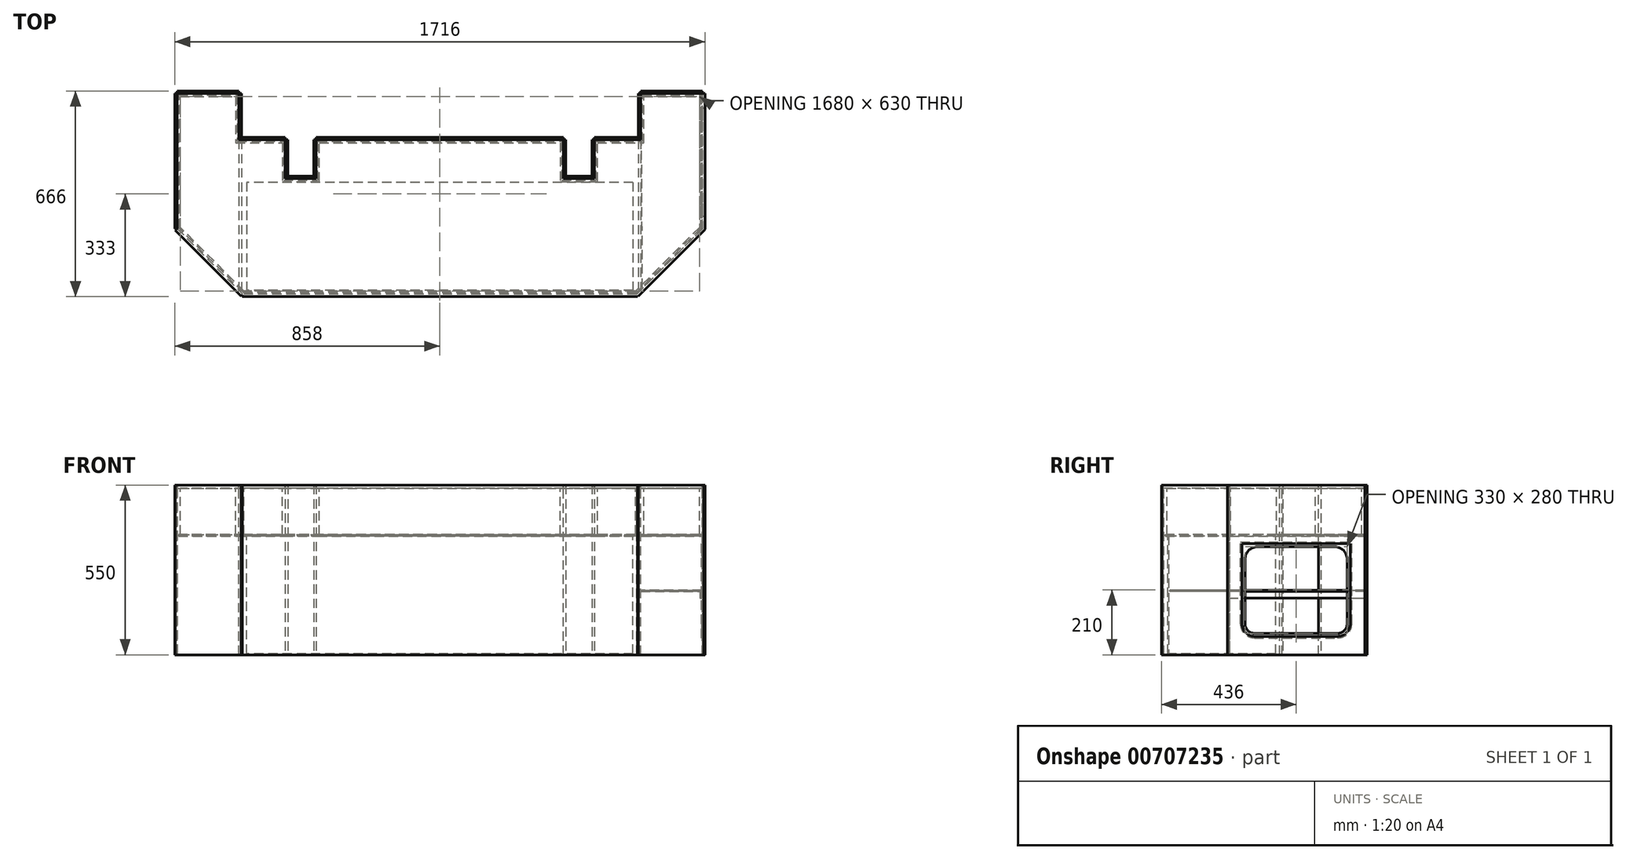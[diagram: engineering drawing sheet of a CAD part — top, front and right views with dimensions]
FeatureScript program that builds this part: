
annotation { "Feature Type Name" : "Feature", "Feature Type Description" : "" }
export const myFeature = defineFeature(function(context is Context, id is Id, definition is map)
    precondition{}
    {
        {
            var Q0;
            Q0=qCreatedBy(makeId("Top.planeOp"),FACE);
            var sketch = newSketch(context, id + "F0", { "sketchPlane" : qUnion([Q0])});
            skLineSegment(sketch, "E0.bottom", {"start": v(650, 250) * mm, "end": v(500, 250) * mm});
            skLineSegment(sketch, "E0.top", {"start": v(637.5, -250) * mm, "end": v(-637.5, -250) * mm});
            skLineSegment(sketch, "E0.left", {"start": v(850, 250) * mm, "end": v(850, -37.5) * mm});
            skLineSegment(sketch, "E0.right", {"start": v(-850, 250) * mm, "end": v(-850, -37.5) * mm});
            skPoint(sketch, "E0.middle", {"position": v(0, 0) * mm});
            skLineSegment(sketch, "E1.top", {"start": v(-850, 400) * mm, "end": v(-650, 400) * mm});
            skLineSegment(sketch, "E1.left", {"start": v(-850, 250) * mm, "end": v(-850, 400) * mm});
            skLineSegment(sketch, "E1.right", {"start": v(-650, 250) * mm, "end": v(-650, 400) * mm});
            skLineSegment(sketch, "E2", {"start": v(0, 547.12) * mm, "end": v(0, -339.99) * mm, "construction": true});
            skLineSegment(sketch, "E3.MirrorCS", {"start": v(850, 250) * mm, "end": v(850, 400) * mm});
            skLineSegment(sketch, "E4.MirrorCS", {"start": v(850, 400) * mm, "end": v(650, 400) * mm});
            skLineSegment(sketch, "E5.MirrorCS", {"start": v(650, 250) * mm, "end": v(650, 400) * mm});
            skLineSegment(sketch, "E6", {"start": v(-400, 250) * mm, "end": v(-400, 125) * mm});
            skLineSegment(sketch, "E7", {"start": v(-400, 125) * mm, "end": v(-500, 125) * mm});
            skLineSegment(sketch, "E8", {"start": v(-500, 125) * mm, "end": v(-500, 250) * mm});
            skLineSegment(sketch, "E9.MirrorCS", {"start": v(400, 250) * mm, "end": v(400, 125) * mm});
            skLineSegment(sketch, "E10.MirrorCS", {"start": v(400, 125) * mm, "end": v(500, 125) * mm});
            skLineSegment(sketch, "E11.MirrorCS", {"start": v(500, 125) * mm, "end": v(500, 250) * mm});
            skLineSegment(sketch, "E12", {"start": v(637.5, -62.5) * mm, "end": v(-637.5, -62.5) * mm, "construction": true});
            skLineSegment(sketch, "E13.top", {"start": v(900, -250) * mm, "end": v(850, -250) * mm, "construction": true});
            skPoint(sketch, "E13.middle", {"position": v(0, -62.5) * mm});
            skLineSegment(sketch, "E14", {"start": v(637.5, 90) * mm, "end": v(637.5, -250) * mm, "construction": true});
            skLineSegment(sketch, "E15", {"start": v(-637.5, 90) * mm, "end": v(-637.5, -250) * mm, "construction": true});
            skLineSegment(sketch, "E16.trimOffspring", {"start": v(400, 250) * mm, "end": v(-400, 250) * mm});
            skLineSegment(sketch, "E17.trimOffspring", {"start": v(-500, 250) * mm, "end": v(-650, 250) * mm});
            skPoint(sketch, "E18.orphan", {"position": v(-850, -250) * mm});
            skLineSegment(sketch, "E19.trimOffspring", {"start": v(637.5, -250) * mm, "end": v(-500, -250) * mm, "construction": true});
            skLineSegment(sketch, "E20", {"start": v(-850, -37.5) * mm, "end": v(-637.5, -250) * mm});
            skLineSegment(sketch, "E21", {"start": v(637.5, -250) * mm, "end": v(850, -37.5) * mm});
            skSolve(sketch);
        }
        {
            var Q0;
            Q0=makeQuery(id+"F0.imprint","IMPRINT",FACE,{"disambiguationData":[TD([[makeQuery(id+"F0.imprint","IMPRINT",EDGE,{"derivedFrom":sQuery(id+"F0.wireOp",EDGE,"E0.bottom")}),1.0]])]});
            extrude(context, id + "F1", {"entities" : qUnion([Q0]), "oppositeDirection" : true, "depth" : 10 * mm, "offsetDistance" : 25 * mm});
        }
        {
            var Q0;
            Q0=makeQuery(id+"F1.opExtrude","CAP_FACE",FACE,{"disambiguationData":[OSD([sQuery(id+"F0.wireOp",EDGE,"E0.bottom"),sQuery(id+"F0.wireOp",EDGE,"E0.top"),sQuery(id+"F0.wireOp",EDGE,"E0.left"),sQuery(id+"F0.wireOp",EDGE,"E0.right"),sQuery(id+"F0.wireOp",EDGE,"E1.top"),sQuery(id+"F0.wireOp",EDGE,"E1.left"),sQuery(id+"F0.wireOp",EDGE,"E1.right"),sQuery(id+"F0.wireOp",EDGE,"E3.MirrorCS"),sQuery(id+"F0.wireOp",EDGE,"E4.MirrorCS"),sQuery(id+"F0.wireOp",EDGE,"E5.MirrorCS"),sQuery(id+"F0.wireOp",EDGE,"E6"),sQuery(id+"F0.wireOp",EDGE,"E7"),sQuery(id+"F0.wireOp",EDGE,"E8"),sQuery(id+"F0.wireOp",EDGE,"E9.MirrorCS"),sQuery(id+"F0.wireOp",EDGE,"E10.MirrorCS"),sQuery(id+"F0.wireOp",EDGE,"E11.MirrorCS"),sQuery(id+"F0.wireOp",EDGE,"E16.trimOffspring"),sQuery(id+"F0.wireOp",EDGE,"E17.trimOffspring"),sQuery(id+"F0.wireOp",EDGE,"E20"),sQuery(id+"F0.wireOp",EDGE,"E21")])],"isStart":false});
            var sketch = newSketch(context, id + "F2", { "sketchPlane" : qUnion([Q0])});
            skLineSegment(sketch, "E22.0", {"start": v(-633.36, 240) * mm, "end": v(-840, 33.36) * mm});
            skLineSegment(sketch, "E22.1", {"start": v(633.36, 240) * mm, "end": v(-633.36, 240) * mm});
            skLineSegment(sketch, "E22.2", {"start": v(840, 33.36) * mm, "end": v(633.36, 240) * mm});
            skLineSegment(sketch, "E22.3", {"start": v(840, -390) * mm, "end": v(840, 33.36) * mm});
            skLineSegment(sketch, "E22.4", {"start": v(660, -390) * mm, "end": v(840, -390) * mm});
            skLineSegment(sketch, "E22.5", {"start": v(-840, 33.36) * mm, "end": v(-840, -390) * mm});
            skLineSegment(sketch, "E22.6", {"start": v(660, -240) * mm, "end": v(660, -390) * mm});
            skLineSegment(sketch, "E22.7", {"start": v(510, -240) * mm, "end": v(660, -240) * mm});
            skLineSegment(sketch, "E22.8", {"start": v(-510, -240) * mm, "end": v(-510, -115) * mm});
            skLineSegment(sketch, "E22.9", {"start": v(-660, -240) * mm, "end": v(-510, -240) * mm});
            skLineSegment(sketch, "E22.10", {"start": v(-660, -390) * mm, "end": v(-660, -240) * mm});
            skLineSegment(sketch, "E22.11", {"start": v(-840, -390) * mm, "end": v(-660, -390) * mm});
            skLineSegment(sketch, "E22.12", {"start": v(-510, -115) * mm, "end": v(-390, -115) * mm});
            skLineSegment(sketch, "E22.13", {"start": v(-390, -115) * mm, "end": v(-390, -240) * mm});
            skLineSegment(sketch, "E22.14", {"start": v(-390, -240) * mm, "end": v(390, -240) * mm});
            skLineSegment(sketch, "E22.15", {"start": v(390, -240) * mm, "end": v(390, -115) * mm});
            skLineSegment(sketch, "E22.16", {"start": v(390, -115) * mm, "end": v(510, -115) * mm});
            skLineSegment(sketch, "E22.17", {"start": v(510, -115) * mm, "end": v(510, -240) * mm});
            skSolve(sketch);
        }
        {
            var Q0;
            Q0 = qSketchRegion(id + "F2", true);
            extrude(context, id + "F3", {"entities" : qUnion([Q0]), "operationType" : NewBodyOperationType.ADD, "depth" : 150 * mm, "offsetDistance" : 25 * mm});
        }
        {
            var Q0;
            Q0=makeQuery(id+"F3.opExtrude","CAP_FACE",FACE,{"disambiguationData":[OSD([sQuery(id+"F2.wireOp",EDGE,"E22.0"),sQuery(id+"F2.wireOp",EDGE,"E22.1"),sQuery(id+"F2.wireOp",EDGE,"E22.2"),sQuery(id+"F2.wireOp",EDGE,"E22.3"),sQuery(id+"F2.wireOp",EDGE,"E22.4"),sQuery(id+"F2.wireOp",EDGE,"E22.5"),sQuery(id+"F2.wireOp",EDGE,"E22.6"),sQuery(id+"F2.wireOp",EDGE,"E22.7"),sQuery(id+"F2.wireOp",EDGE,"E22.8"),sQuery(id+"F2.wireOp",EDGE,"E22.9"),sQuery(id+"F2.wireOp",EDGE,"E22.10"),sQuery(id+"F2.wireOp",EDGE,"E22.11"),sQuery(id+"F2.wireOp",EDGE,"E22.12"),sQuery(id+"F2.wireOp",EDGE,"E22.13"),sQuery(id+"F2.wireOp",EDGE,"E22.14"),sQuery(id+"F2.wireOp",EDGE,"E22.15"),sQuery(id+"F2.wireOp",EDGE,"E22.16"),sQuery(id+"F2.wireOp",EDGE,"E22.17")])],"isStart":false});
            var sketch = newSketch(context, id + "F4", { "sketchPlane" : qUnion([Q0])});
            skLineSegment(sketch, "E23.0", {"start": v(845, 35.43) * mm, "end": v(635.43, 245) * mm});
            skLineSegment(sketch, "E23.1", {"start": v(845, -395) * mm, "end": v(845, 35.43) * mm});
            skLineSegment(sketch, "E23.2", {"start": v(655, -395) * mm, "end": v(845, -395) * mm});
            skLineSegment(sketch, "E23.3", {"start": v(655, -245) * mm, "end": v(655, -395) * mm});
            skLineSegment(sketch, "E23.4", {"start": v(505, -245) * mm, "end": v(655, -245) * mm});
            skLineSegment(sketch, "E23.5", {"start": v(635.43, 245) * mm, "end": v(-635.43, 245) * mm});
            skLineSegment(sketch, "E23.6", {"start": v(505, -120) * mm, "end": v(505, -245) * mm});
            skLineSegment(sketch, "E23.7", {"start": v(395, -120) * mm, "end": v(505, -120) * mm});
            skLineSegment(sketch, "E23.8", {"start": v(-655, -395) * mm, "end": v(-655, -245) * mm});
            skLineSegment(sketch, "E23.9", {"start": v(-845, -395) * mm, "end": v(-655, -395) * mm});
            skLineSegment(sketch, "E23.10", {"start": v(-845, 35.43) * mm, "end": v(-845, -395) * mm});
            skLineSegment(sketch, "E23.11", {"start": v(-635.43, 245) * mm, "end": v(-845, 35.43) * mm});
            skLineSegment(sketch, "E23.12", {"start": v(-655, -245) * mm, "end": v(-505, -245) * mm});
            skLineSegment(sketch, "E23.13", {"start": v(-505, -245) * mm, "end": v(-505, -120) * mm});
            skLineSegment(sketch, "E23.14", {"start": v(-505, -120) * mm, "end": v(-395, -120) * mm});
            skLineSegment(sketch, "E23.15", {"start": v(-395, -120) * mm, "end": v(-395, -245) * mm});
            skLineSegment(sketch, "E23.16", {"start": v(-395, -245) * mm, "end": v(395, -245) * mm});
            skLineSegment(sketch, "E23.17", {"start": v(395, -245) * mm, "end": v(395, -120) * mm});
            skSolve(sketch);
        }
        {
            var Q0;
            Q0 = qSketchRegion(id + "F4", true);
            extrude(context, id + "F5", {"entities" : qUnion([Q0]), "operationType" : NewBodyOperationType.ADD, "depth" : 6 * mm, "offsetDistance" : 25 * mm});
        }
        {
            var Q0;
            Q0=makeQuery(id+"F1.opExtrude","SWEPT_FACE",FACE,{"disambiguationData":[OSD([sQuery(id+"F0.wireOp",EDGE,"E0.right"),sQuery(id+"F0.wireOp",EDGE,"E1.left")])]});
            var sketch = newSketch(context, id + "F6", { "sketchPlane" : qUnion([Q0])});
            skLineSegment(sketch, "E24.bottom", {"start": v(-400, 0) * mm, "end": v(37.5, 0) * mm});
            skLineSegment(sketch, "E24.top", {"start": v(-400, -550) * mm, "end": v(37.5, -550) * mm});
            skLineSegment(sketch, "E24.left", {"start": v(-400, 0) * mm, "end": v(-400, -550) * mm});
            skLineSegment(sketch, "E24.right", {"start": v(37.5, 0) * mm, "end": v(37.5, -550) * mm});
            skSolve(sketch);
        }
        {
            var Q0;
            Q0 = qSketchRegion(id + "F6", true);
            extrude(context, id + "F7", {"entities" : qUnion([Q0]), "depth" : 8 * mm, "offsetDistance" : 25 * mm});
        }
        {
            var Q0;
            Q0=makeQuery(id+"F1.opExtrude","SWEPT_FACE",FACE,{"disambiguationData":[OSD([sQuery(id+"F0.wireOp",EDGE,"E20")])]});
            var sketch = newSketch(context, id + "F8", { "sketchPlane" : qUnion([Q0])});
            skLineSegment(sketch, "E25.bottom", {"start": v(-574.52, 0) * mm, "end": v(-274, 0) * mm});
            skLineSegment(sketch, "E25.top", {"start": v(-574.52, -550) * mm, "end": v(-274, -550) * mm});
            skLineSegment(sketch, "E25.left", {"start": v(-574.52, 0) * mm, "end": v(-574.52, -550) * mm});
            skLineSegment(sketch, "E25.right", {"start": v(-274, 0) * mm, "end": v(-274, -550) * mm});
            skSolve(sketch);
        }
        {
            var Q0;
            Q0 = qSketchRegion(id + "F8", true);
            extrude(context, id + "F9", {"entities" : qUnion([Q0]), "operationType" : NewBodyOperationType.ADD, "depth" : 8 * mm, "offsetDistance" : 25 * mm});
        }
        {
            var Q0;
            Q0=makeQuery(id+"F1.opExtrude","SWEPT_FACE",FACE,{"disambiguationData":[OSD([sQuery(id+"F0.wireOp",EDGE,"E0.top")])]});
            var sketch = newSketch(context, id + "F10", { "sketchPlane" : qUnion([Q0])});
            skLineSegment(sketch, "E26.bottom", {"start": v(-639.5, 0) * mm, "end": v(635.5, 0) * mm});
            skLineSegment(sketch, "E26.top", {"start": v(-639.5, -550) * mm, "end": v(639.5, -550) * mm});
            skLineSegment(sketch, "E26.left", {"start": v(-639.5, 0) * mm, "end": v(-639.5, -550) * mm});
            skLineSegment(sketch, "E26.right", {"start": v(639.5, 0) * mm, "end": v(639.5, -550) * mm});
            skLineSegment(sketch, "E27", {"start": v(0, 0) * mm, "end": v(0, -550) * mm, "construction": true});
            skLineSegment(sketch, "E28", {"start": v(637.5, 0) * mm, "end": v(-637.5, 0) * mm});
            skLineSegment(sketch, "E29", {"start": v(639.5, 0) * mm, "end": v(-637.5, 0) * mm});
            skSolve(sketch);
        }
        {
            var Q0;
            Q0 = qSketchRegion(id + "F10", true);
            extrude(context, id + "F11", {"entities" : qUnion([Q0]), "depth" : 8 * mm, "offsetDistance" : 25 * mm});
        }
        {
            var Q0;
            Q0=makeQuery(id+"F1.opExtrude","SWEPT_FACE",FACE,{"disambiguationData":[OSD([sQuery(id+"F0.wireOp",EDGE,"E21")])]});
            var sketch = newSketch(context, id + "F12", { "sketchPlane" : qUnion([Q0])});
            skLineSegment(sketch, "E30.top", {"start": v(272.52, -550) * mm, "end": v(574.52, -550) * mm});
            skLineSegment(sketch, "E31", {"start": v(272.52, 0) * mm, "end": v(574.52, 0) * mm});
            skLineSegment(sketch, "E32", {"start": v(574.52, 0) * mm, "end": v(574.52, -550) * mm});
            skLineSegment(sketch, "E33", {"start": v(272.52, -550) * mm, "end": v(272.52, 0) * mm});
            skSolve(sketch);
        }
        {
            var Q0;
            Q0 = qSketchRegion(id + "F12", true);
            extrude(context, id + "F13", {"entities" : qUnion([Q0]), "operationType" : NewBodyOperationType.ADD, "depth" : 8 * mm, "offsetDistance" : 25 * mm});
        }
        {
            var Q0;
            Q0=makeQuery(id+"F1.opExtrude","SWEPT_FACE",FACE,{"disambiguationData":[OSD([sQuery(id+"F0.wireOp",EDGE,"E0.left"),sQuery(id+"F0.wireOp",EDGE,"E3.MirrorCS")])]});
            var sketch = newSketch(context, id + "F14", { "sketchPlane" : qUnion([Q0])});
            skLineSegment(sketch, "E34.bottom", {"start": v(-44, 0) * mm, "end": v(400, 0) * mm});
            skLineSegment(sketch, "E34.top", {"start": v(-44, -550) * mm, "end": v(400, -550) * mm});
            skLineSegment(sketch, "E34.left", {"start": v(-44, 0) * mm, "end": v(-44, -550) * mm});
            skLineSegment(sketch, "E34.right", {"start": v(400, 0) * mm, "end": v(400, -550) * mm});
            skSolve(sketch);
        }
        {
            var Q0;
            Q0 = qSketchRegion(id + "F14", true);
            extrude(context, id + "F15", {"entities" : qUnion([Q0]), "operationType" : NewBodyOperationType.ADD, "depth" : 8 * mm, "offsetDistance" : 25 * mm});
        }
        {
            var Q0;
            Q0=makeQuery(id+"F1.opExtrude","SWEPT_FACE",FACE,{"disambiguationData":[OSD([sQuery(id+"F0.wireOp",EDGE,"E1.top")])]});
            var sketch = newSketch(context, id + "F16", { "sketchPlane" : qUnion([Q0])});
            skLineSegment(sketch, "E35.bottom", {"start": v(850, 0) * mm, "end": v(650, 0) * mm});
            skLineSegment(sketch, "E35.top", {"start": v(850, -550) * mm, "end": v(650, -550) * mm});
            skLineSegment(sketch, "E35.left", {"start": v(850, 0) * mm, "end": v(850, -550) * mm});
            skLineSegment(sketch, "E35.right", {"start": v(650, 0) * mm, "end": v(650, -550) * mm});
            skSolve(sketch);
        }
        {
            var Q0;
            Q0 = qSketchRegion(id + "F16", true);
            extrude(context, id + "F17", {"entities" : qUnion([Q0]), "depth" : 8 * mm, "offsetDistance" : 25 * mm});
        }
        {
            var Q0;
            Q0=makeQuery(id+"F1.opExtrude","SWEPT_FACE",FACE,{"disambiguationData":[OSD([sQuery(id+"F0.wireOp",EDGE,"E1.right")])]});
            var sketch = newSketch(context, id + "F18", { "sketchPlane" : qUnion([Q0])});
            skLineSegment(sketch, "E36.bottom", {"start": v(250, 0) * mm, "end": v(400, 0) * mm});
            skLineSegment(sketch, "E36.top", {"start": v(250, -550) * mm, "end": v(400, -550) * mm});
            skLineSegment(sketch, "E36.left", {"start": v(250, 0) * mm, "end": v(250, -550) * mm});
            skLineSegment(sketch, "E36.right", {"start": v(400, 0) * mm, "end": v(400, -550) * mm});
            skSolve(sketch);
        }
        {
            var Q0;
            Q0 = qSketchRegion(id + "F18", true);
            extrude(context, id + "F19", {"entities" : qUnion([Q0]), "depth" : 8 * mm, "offsetDistance" : 25 * mm});
        }
        {
            var Q0;
            Q0=makeQuery(id+"F1.opExtrude","SWEPT_FACE",FACE,{"disambiguationData":[OSD([sQuery(id+"F0.wireOp",EDGE,"E17.trimOffspring")])]});
            var sketch = newSketch(context, id + "F20", { "sketchPlane" : qUnion([Q0])});
            skLineSegment(sketch, "E37.bottom", {"start": v(500, 0) * mm, "end": v(642.04, 0) * mm});
            skLineSegment(sketch, "E37.top", {"start": v(500, -550) * mm, "end": v(642.04, -550) * mm});
            skLineSegment(sketch, "E37.left", {"start": v(500, 0) * mm, "end": v(500, -550) * mm});
            skLineSegment(sketch, "E37.right", {"start": v(642.04, 0) * mm, "end": v(642.04, -550) * mm});
            skSolve(sketch);
        }
        {
            var Q0;
            Q0 = qSketchRegion(id + "F20", true);
            extrude(context, id + "F21", {"entities" : qUnion([Q0]), "depth" : 8 * mm, "offsetDistance" : 25 * mm});
        }
        {
            var Q0;
            Q0=makeQuery(id+"F1.opExtrude","SWEPT_FACE",FACE,{"disambiguationData":[OSD([sQuery(id+"F0.wireOp",EDGE,"E7")])]});
            var sketch = newSketch(context, id + "F22", { "sketchPlane" : qUnion([Q0])});
            skLineSegment(sketch, "E38.bottom", {"start": v(500, 0) * mm, "end": v(400, 0) * mm});
            skLineSegment(sketch, "E38.top", {"start": v(500, -550) * mm, "end": v(400, -550) * mm});
            skLineSegment(sketch, "E38.left", {"start": v(500, 0) * mm, "end": v(500, -550) * mm});
            skLineSegment(sketch, "E38.right", {"start": v(400, 0) * mm, "end": v(400, -550) * mm});
            skSolve(sketch);
        }
        {
            var Q0;
            Q0 = qSketchRegion(id + "F22", true);
            extrude(context, id + "F23", {"entities" : qUnion([Q0]), "depth" : 8 * mm, "offsetDistance" : 25 * mm});
        }
        {
            var Q0;
            Q0=makeQuery(id+"F1.opExtrude","SWEPT_FACE",FACE,{"disambiguationData":[OSD([sQuery(id+"F0.wireOp",EDGE,"E8")])]});
            var sketch = newSketch(context, id + "F24", { "sketchPlane" : qUnion([Q0])});
            skLineSegment(sketch, "E39.bottom", {"start": v(250, 0) * mm, "end": v(135, 0) * mm});
            skLineSegment(sketch, "E39.top", {"start": v(250, -550) * mm, "end": v(135, -550) * mm});
            skLineSegment(sketch, "E39.left", {"start": v(250, 0) * mm, "end": v(250, -550) * mm});
            skLineSegment(sketch, "E39.right", {"start": v(135, 0) * mm, "end": v(135, -550) * mm});
            skSolve(sketch);
        }
        {
            var Q0;
            Q0 = qSketchRegion(id + "F24", true);
            extrude(context, id + "F25", {"entities" : qUnion([Q0]), "depth" : 8 * mm, "offsetDistance" : 25 * mm});
        }
        {
            var Q0;
            Q0=makeQuery(id+"F1.opExtrude","SWEPT_FACE",FACE,{"disambiguationData":[OSD([sQuery(id+"F0.wireOp",EDGE,"E6")])]});
            var sketch = newSketch(context, id + "F26", { "sketchPlane" : qUnion([Q0])});
            skLineSegment(sketch, "E40.bottom", {"start": v(-250, 0) * mm, "end": v(-135, 0) * mm});
            skLineSegment(sketch, "E40.top", {"start": v(-250, -550) * mm, "end": v(-135, -550) * mm});
            skLineSegment(sketch, "E40.left", {"start": v(-250, 0) * mm, "end": v(-250, -550) * mm});
            skLineSegment(sketch, "E40.right", {"start": v(-135, 0) * mm, "end": v(-135, -550) * mm});
            skSolve(sketch);
        }
        {
            var Q0;
            Q0 = qSketchRegion(id + "F26", true);
            extrude(context, id + "F27", {"entities" : qUnion([Q0]), "depth" : 8 * mm, "offsetDistance" : 25 * mm});
        }
        {
            var Q0;
            Q0=makeQuery(id+"F17.opExtrude","SWEPT_BODY",BODY,{"disambiguationData":[OSD([sQuery(id+"F16.wireOp",EDGE,"E35.bottom"),sQuery(id+"F16.wireOp",EDGE,"E35.top"),sQuery(id+"F16.wireOp",EDGE,"E35.left"),sQuery(id+"F16.wireOp",EDGE,"E35.right")])]});
            var Q1;
            Q1=makeQuery(id+"F19.opExtrude","SWEPT_BODY",BODY,{"disambiguationData":[OSD([sQuery(id+"F18.wireOp",EDGE,"E36.bottom"),sQuery(id+"F18.wireOp",EDGE,"E36.top"),sQuery(id+"F18.wireOp",EDGE,"E36.left"),sQuery(id+"F18.wireOp",EDGE,"E36.right")])]});
            var Q2;
            Q2=makeQuery(id+"F21.opExtrude","SWEPT_BODY",BODY,{"disambiguationData":[OSD([sQuery(id+"F20.wireOp",EDGE,"E37.bottom"),sQuery(id+"F20.wireOp",EDGE,"E37.top"),sQuery(id+"F20.wireOp",EDGE,"E37.left"),sQuery(id+"F20.wireOp",EDGE,"E37.right")])]});
            var Q3;
            Q3=makeQuery(id+"F25.opExtrude","SWEPT_BODY",BODY,{"disambiguationData":[OSD([sQuery(id+"F24.wireOp",EDGE,"E39.bottom"),sQuery(id+"F24.wireOp",EDGE,"E39.top"),sQuery(id+"F24.wireOp",EDGE,"E39.left"),sQuery(id+"F24.wireOp",EDGE,"E39.right")])]});
            var Q4;
            Q4=makeQuery(id+"F23.opExtrude","SWEPT_BODY",BODY,{"disambiguationData":[OSD([sQuery(id+"F22.wireOp",EDGE,"E38.bottom"),sQuery(id+"F22.wireOp",EDGE,"E38.top"),sQuery(id+"F22.wireOp",EDGE,"E38.left"),sQuery(id+"F22.wireOp",EDGE,"E38.right")])]});
            var Q5;
            Q5=makeQuery(id+"F27.opExtrude","SWEPT_BODY",BODY,{"disambiguationData":[OSD([sQuery(id+"F26.wireOp",EDGE,"E40.bottom"),sQuery(id+"F26.wireOp",EDGE,"E40.top"),sQuery(id+"F26.wireOp",EDGE,"E40.left"),sQuery(id+"F26.wireOp",EDGE,"E40.right")])]});
            var Q6;
            Q6=qCreatedBy(makeId("Right.planeOp"),FACE);
            mirror(context, id + "F28", {"entities" : qUnion([Q0, Q1, Q2, Q3, Q4, Q5]), "mirrorPlane" : qUnion([Q6])});
        }
        {
            var Q0;
            Q0=makeQuery(id+"F1.opExtrude","SWEPT_FACE",FACE,{"disambiguationData":[OSD([sQuery(id+"F0.wireOp",EDGE,"E16.trimOffspring")])]});
            var sketch = newSketch(context, id + "F29", { "sketchPlane" : qUnion([Q0])});
            skLineSegment(sketch, "E41.bottom", {"start": v(400, 0) * mm, "end": v(-400, 0) * mm});
            skLineSegment(sketch, "E41.top", {"start": v(400, -550) * mm, "end": v(-400, -550) * mm});
            skLineSegment(sketch, "E41.left", {"start": v(400, 0) * mm, "end": v(400, -550) * mm});
            skLineSegment(sketch, "E41.right", {"start": v(-400, 0) * mm, "end": v(-400, -550) * mm});
            skSolve(sketch);
        }
        {
            var Q0;
            Q0 = qSketchRegion(id + "F29", true);
            extrude(context, id + "F30", {"entities" : qUnion([Q0]), "depth" : 8 * mm, "offsetDistance" : 25 * mm});
        }
        {
            var Q0;
            Q0=makeQuery(id+"F19.opExtrude","CAP_FACE",FACE,{"disambiguationData":[OSD([sQuery(id+"F18.wireOp",EDGE,"E36.bottom"),sQuery(id+"F18.wireOp",EDGE,"E36.top"),sQuery(id+"F18.wireOp",EDGE,"E36.left"),sQuery(id+"F18.wireOp",EDGE,"E36.right")])],"isStart":true});
            var sketch = newSketch(context, id + "F31", { "sketchPlane" : qUnion([Q0])});
            skLineSegment(sketch, "E42.bottom", {"start": v(-250, -165) * mm, "end": v(235, -165) * mm});
            skLineSegment(sketch, "E42.top", {"start": v(-250, -550) * mm, "end": v(235, -550) * mm});
            skLineSegment(sketch, "E42.left", {"start": v(-250, -165) * mm, "end": v(-250, -550) * mm});
            skLineSegment(sketch, "E42.right", {"start": v(235, -165) * mm, "end": v(235, -550) * mm});
            skSolve(sketch);
        }
        {
            var Q0;
            Q0 = qSketchRegion(id + "F31", true);
            extrude(context, id + "F32", {"entities" : qUnion([Q0]), "oppositeDirection" : true, "depth" : 8 * mm, "offsetDistance" : 25 * mm});
        }
        {
            var Q0;
            Q0=makeQuery(id+"F32.opExtrude","SWEPT_BODY",BODY,{"disambiguationData":[OSD([sQuery(id+"F31.wireOp",EDGE,"E42.bottom"),sQuery(id+"F31.wireOp",EDGE,"E42.top"),sQuery(id+"F31.wireOp",EDGE,"E42.left"),sQuery(id+"F31.wireOp",EDGE,"E42.right")])]});
            var Q1;
            Q1=qCreatedBy(makeId("Right.planeOp"),FACE);
            mirror(context, id + "F33", {"entities" : qUnion([Q0]), "mirrorPlane" : qUnion([Q1])});
        }
        {
            var Q0;
            Q0=makeQuery(id+"F15.opExtrude","CAP_FACE",FACE,{"disambiguationData":[OSD([sQuery(id+"F14.wireOp",EDGE,"E34.bottom"),sQuery(id+"F14.wireOp",EDGE,"E34.top"),sQuery(id+"F14.wireOp",EDGE,"E34.left"),sQuery(id+"F14.wireOp",EDGE,"E34.right")])],"isStart":false});
            var sketch = newSketch(context, id + "F34", { "sketchPlane" : qUnion([Q0])});
            skLineSegment(sketch, "E43", {"start": v(178, -550) * mm, "end": v(178, 0) * mm, "construction": true});
            skLineSegment(sketch, "E44.bottom", {"start": v(43, -490) * mm, "end": v(313, -490) * mm});
            skLineSegment(sketch, "E44.top", {"start": v(3, -190) * mm, "end": v(353, -190) * mm});
            skLineSegment(sketch, "E44.left", {"start": v(3, -450) * mm, "end": v(3, -190) * mm});
            skLineSegment(sketch, "E44.right", {"start": v(353, -450) * mm, "end": v(353, -190) * mm});
            skPoint(sketch, "E44.middle", {"position": v(178, -340) * mm});
            skPoint(sketch, "E45.visualSharp", {"position": v(353, -490) * mm});
            skArc(sketch, "E45.filletArc", {"start": v(313, -490) * mm, "mid": v(341.28, -478.28) * mm, "end": v(353, -450) * mm});
            skPoint(sketch, "E46.visualSharp", {"position": v(3, -490) * mm});
            skArc(sketch, "E46.filletArc", {"start": v(3, -450) * mm, "mid": v(14.72, -478.28) * mm, "end": v(43, -490) * mm});
            skSolve(sketch);
        }
        {
            var Q0;
            Q0 = qSketchRegion(id + "F34", true);
            extrude(context, id + "F35", {"entities" : qUnion([Q0]), "operationType" : NewBodyOperationType.REMOVE, "oppositeDirection" : true, "depth" : 25 * mm, "offsetDistance" : 25 * mm});
        }
        {
            var Q0;
            Q0=makeQuery(id+"F15.opExtrude","CAP_FACE",FACE,{"disambiguationData":[OSD([sQuery(id+"F14.wireOp",EDGE,"E34.bottom"),sQuery(id+"F14.wireOp",EDGE,"E34.top"),sQuery(id+"F14.wireOp",EDGE,"E34.left"),sQuery(id+"F14.wireOp",EDGE,"E34.right")])],"isStart":true});
            var sketch = newSketch(context, id + "F36", { "sketchPlane" : qUnion([Q0])});
            skArc(sketch, "E47.0", {"start": v(-13, -450) * mm, "mid": v(-21.79, -471.21) * mm, "end": v(-43, -480) * mm});
            skArc(sketch, "E47.1", {"start": v(-313, -480) * mm, "mid": v(-334.21, -471.21) * mm, "end": v(-343, -450) * mm});
            skLineSegment(sketch, "E47.2", {"start": v(-343, -450) * mm, "end": v(-343, -240) * mm});
            skLineSegment(sketch, "E47.3", {"start": v(-43, -480) * mm, "end": v(-313, -480) * mm});
            skLineSegment(sketch, "E47.4", {"start": v(-53, -200) * mm, "end": v(-303, -200) * mm});
            skLineSegment(sketch, "E47.5", {"start": v(-13, -450) * mm, "end": v(-13, -240) * mm});
            skArc(sketch, "E48.0", {"start": v(2, -450) * mm, "mid": v(-11.18, -481.82) * mm, "end": v(-43, -495) * mm});
            skArc(sketch, "E48.1", {"start": v(-313, -495) * mm, "mid": v(-344.82, -481.82) * mm, "end": v(-358, -450) * mm});
            skLineSegment(sketch, "E48.2", {"start": v(-358, -450) * mm, "end": v(-358, -185) * mm});
            skLineSegment(sketch, "E48.3", {"start": v(-43, -495) * mm, "end": v(-313, -495) * mm});
            skLineSegment(sketch, "E48.4", {"start": v(2, -185) * mm, "end": v(-358, -185) * mm});
            skLineSegment(sketch, "E48.5", {"start": v(2, -450) * mm, "end": v(2, -185) * mm});
            skPoint(sketch, "E49.visualSharp", {"position": v(-343, -200) * mm});
            skArc(sketch, "E49.filletArc", {"start": v(-303, -200) * mm, "mid": v(-331.28, -211.72) * mm, "end": v(-343, -240) * mm});
            skPoint(sketch, "E50.visualSharp", {"position": v(-13, -200) * mm});
            skArc(sketch, "E50.filletArc", {"start": v(-13, -240) * mm, "mid": v(-24.72, -211.72) * mm, "end": v(-53, -200) * mm});
            skSolve(sketch);
        }
        {
            var Q0;
            Q0 = qSketchRegion(id + "F36", true);
            extrude(context, id + "F37", {"entities" : qUnion([Q0]), "operationType" : NewBodyOperationType.ADD, "depth" : 3 * mm, "offsetDistance" : 25 * mm});
        }
        {
            var Q0;
            Q0=makeQuery(id+"F5.opExtrude","CAP_FACE",FACE,{"disambiguationData":[OSD([sQuery(id+"F4.wireOp",EDGE,"E23.0"),sQuery(id+"F4.wireOp",EDGE,"E23.1"),sQuery(id+"F4.wireOp",EDGE,"E23.2"),sQuery(id+"F4.wireOp",EDGE,"E23.3"),sQuery(id+"F4.wireOp",EDGE,"E23.4"),sQuery(id+"F4.wireOp",EDGE,"E23.5"),sQuery(id+"F4.wireOp",EDGE,"E23.6"),sQuery(id+"F4.wireOp",EDGE,"E23.7"),sQuery(id+"F4.wireOp",EDGE,"E23.8"),sQuery(id+"F4.wireOp",EDGE,"E23.9"),sQuery(id+"F4.wireOp",EDGE,"E23.10"),sQuery(id+"F4.wireOp",EDGE,"E23.11"),sQuery(id+"F4.wireOp",EDGE,"E23.12"),sQuery(id+"F4.wireOp",EDGE,"E23.13"),sQuery(id+"F4.wireOp",EDGE,"E23.14"),sQuery(id+"F4.wireOp",EDGE,"E23.15"),sQuery(id+"F4.wireOp",EDGE,"E23.16"),sQuery(id+"F4.wireOp",EDGE,"E23.17")])],"isStart":false});
            cPlane(context, id + "F38", {"entities" : qUnion([Q0]), "cplaneType" : CPlaneType.OFFSET, "offset" : 175 * mm, "width" : 150 * mm, "height" : 150 * mm});
        }
        {
            var Q0;
            Q0=qCreatedBy(id+"F38.planeOp",FACE);
            var sketch = newSketch(context, id + "F39", { "sketchPlane" : qUnion([Q0])});
            skLineSegment(sketch, "E51.bottom", {"start": v(650.64, -399.43) * mm, "end": v(844.89, -399.43) * mm});
            skLineSegment(sketch, "E51.left", {"start": v(650.64, -399.43) * mm, "end": v(654.42, 231.18) * mm});
            skLineSegment(sketch, "E51.right", {"start": v(844.89, -399.43) * mm, "end": v(847.52, 40.36) * mm});
            skLineSegment(sketch, "E52", {"start": v(847.52, 40.36) * mm, "end": v(654.42, 231.18) * mm});
            skSolve(sketch);
        }
        {
            var Q0;
            Q0 = qSketchRegion(id + "F39", true);
            extrude(context, id + "F40", {"entities" : qUnion([Q0]), "depth" : 3 * mm, "offsetDistance" : 25 * mm});
        }
        {
            var Q0;
            Q0=makeQuery(id+"F40.opExtrude","SWEPT_FACE",FACE,{"disambiguationData":[OSD([sQuery(id+"F39.wireOp",EDGE,"E51.right")])]});
            var sketch = newSketch(context, id + "F41", { "sketchPlane" : qUnion([Q0])});
            skLineSegment(sketch, "E53.bottom", {"start": v(-45.44, -341) * mm, "end": v(394.36, -341) * mm});
            skLineSegment(sketch, "E53.top", {"start": v(-45.44, -366) * mm, "end": v(394.36, -366) * mm});
            skLineSegment(sketch, "E53.left", {"start": v(-45.44, -341) * mm, "end": v(-45.44, -366) * mm});
            skLineSegment(sketch, "E53.right", {"start": v(394.36, -341) * mm, "end": v(394.36, -366) * mm});
            skSolve(sketch);
        }
        {
            var Q0;
            Q0 = qSketchRegion(id + "F41", true);
            extrude(context, id + "F42", {"entities" : qUnion([Q0]), "oppositeDirection" : true, "depth" : 3 * mm, "offsetDistance" : 25 * mm});
        }
        {
            var Q0;
            Q0=makeQuery(id+"F5.opExtrude","CAP_FACE",FACE,{"disambiguationData":[OSD([sQuery(id+"F4.wireOp",EDGE,"E23.0"),sQuery(id+"F4.wireOp",EDGE,"E23.1"),sQuery(id+"F4.wireOp",EDGE,"E23.2"),sQuery(id+"F4.wireOp",EDGE,"E23.3"),sQuery(id+"F4.wireOp",EDGE,"E23.4"),sQuery(id+"F4.wireOp",EDGE,"E23.5"),sQuery(id+"F4.wireOp",EDGE,"E23.6"),sQuery(id+"F4.wireOp",EDGE,"E23.7"),sQuery(id+"F4.wireOp",EDGE,"E23.8"),sQuery(id+"F4.wireOp",EDGE,"E23.9"),sQuery(id+"F4.wireOp",EDGE,"E23.10"),sQuery(id+"F4.wireOp",EDGE,"E23.11"),sQuery(id+"F4.wireOp",EDGE,"E23.12"),sQuery(id+"F4.wireOp",EDGE,"E23.13"),sQuery(id+"F4.wireOp",EDGE,"E23.14"),sQuery(id+"F4.wireOp",EDGE,"E23.15"),sQuery(id+"F4.wireOp",EDGE,"E23.16"),sQuery(id+"F4.wireOp",EDGE,"E23.17")])],"isStart":false});
            var sketch = newSketch(context, id + "F43", { "sketchPlane" : qUnion([Q0])});
            skLineSegment(sketch, "E54.bottom", {"start": v(625, -112.5) * mm, "end": v(-625, -112.5) * mm});
            skLineSegment(sketch, "E54.top", {"start": v(625, 237.5) * mm, "end": v(-625, 237.5) * mm});
            skLineSegment(sketch, "E54.left", {"start": v(625, -112.5) * mm, "end": v(625, 237.5) * mm});
            skLineSegment(sketch, "E54.right", {"start": v(-625, -112.5) * mm, "end": v(-625, 237.5) * mm});
            skSolve(sketch);
        }
        {
            var Q0;
            Q0 = qSketchRegion(id + "F43", true);
            extrude(context, id + "F44", {"entities" : qUnion([Q0]), "depth" : 380 * mm, "offsetDistance" : 25 * mm});
        }
        {
            var Q0;
            Q0=makeQuery(id+"F15.opExtrude","CAP_EDGE",EDGE,{"disambiguationData":[OSD([sQuery(id+"F14.wireOp",EDGE,"E34.left")])],"isStart":false});
            fillet(context, id + "F45", {"entities" : qUnion([Q0]), "radius" : 10 * mm, "tangentPropagation" : true, "allowEdgeOverflow" : false});
        }
    });
